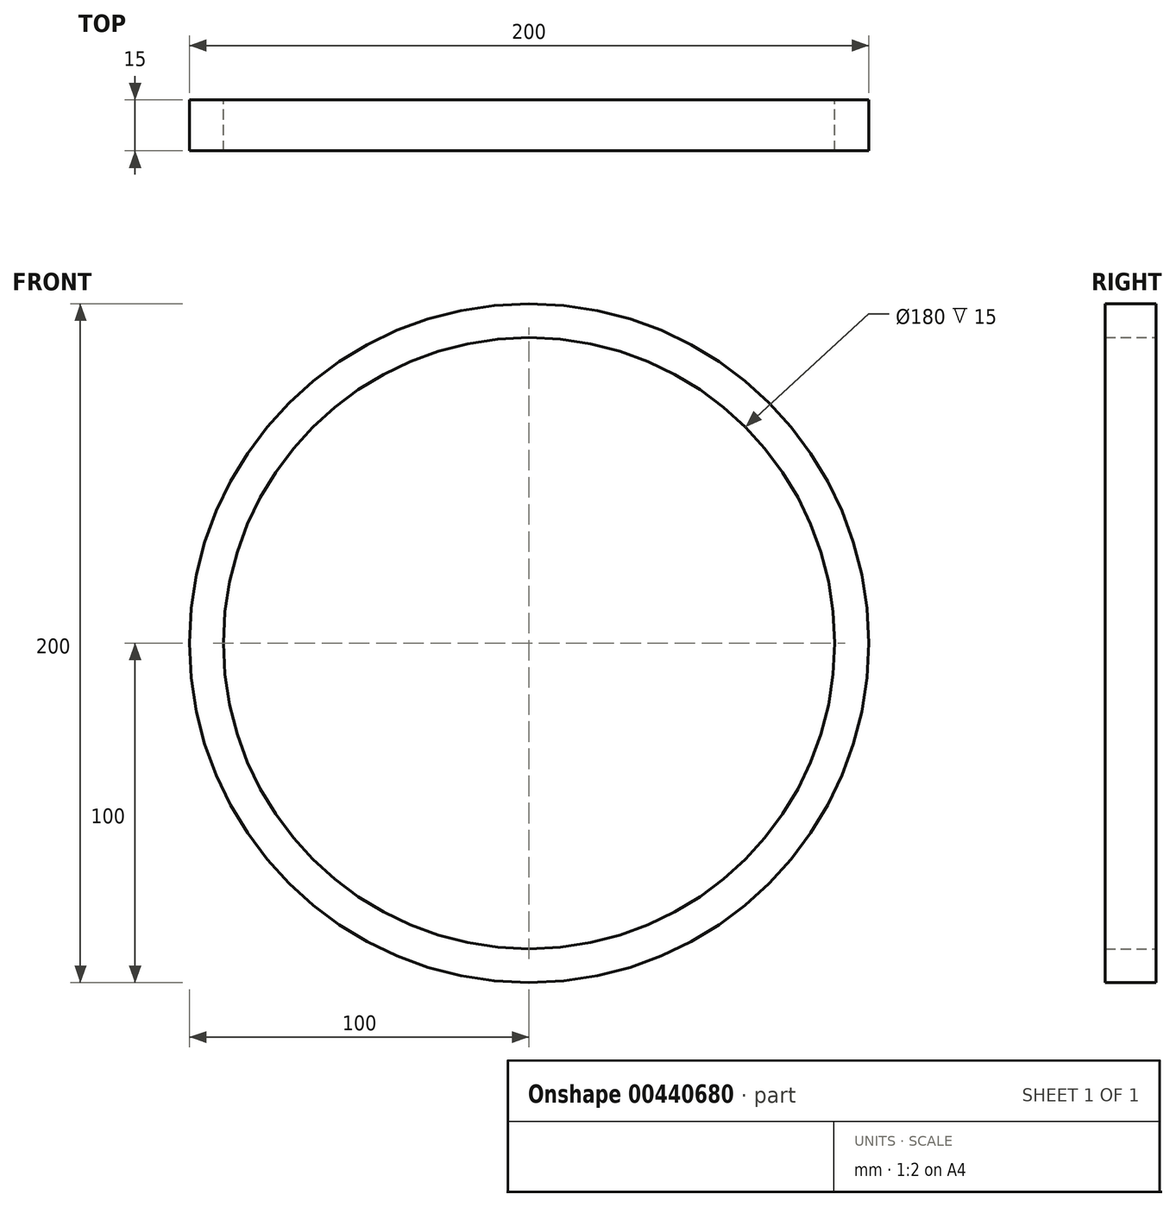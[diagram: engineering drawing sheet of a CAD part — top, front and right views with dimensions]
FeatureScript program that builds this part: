
annotation { "Feature Type Name" : "Feature", "Feature Type Description" : "" }
export const myFeature = defineFeature(function(context is Context, id is Id, definition is map)
    precondition{}
    {
        {
            var Q0;
            Q0=qCreatedBy(makeId("Front.planeOp"),FACE);
            var sketch = newSketch(context, id + "F0", { "sketchPlane" : qUnion([Q0])});
            skCircle(sketch, "E0", {"center": v(0, 0) * mm, "radius": 100 * mm});
            skCircle(sketch, "E1", {"center": v(0, 0) * mm, "radius": 90 * mm});
            skSolve(sketch);
        }
        {
            var Q0;
            Q0=makeQuery(id+"F0.imprint","IMPRINT",FACE,{"disambiguationData":[TD([[makeQuery(id+"F0.imprint","IMPRINT",EDGE,{"derivedFrom":sQuery(id+"F0.wireOp",EDGE,"E0")}),1.0]])]});
            extrude(context, id + "F1", {"entities" : qUnion([Q0]), "depth" : 15 * mm});
        }
    });
